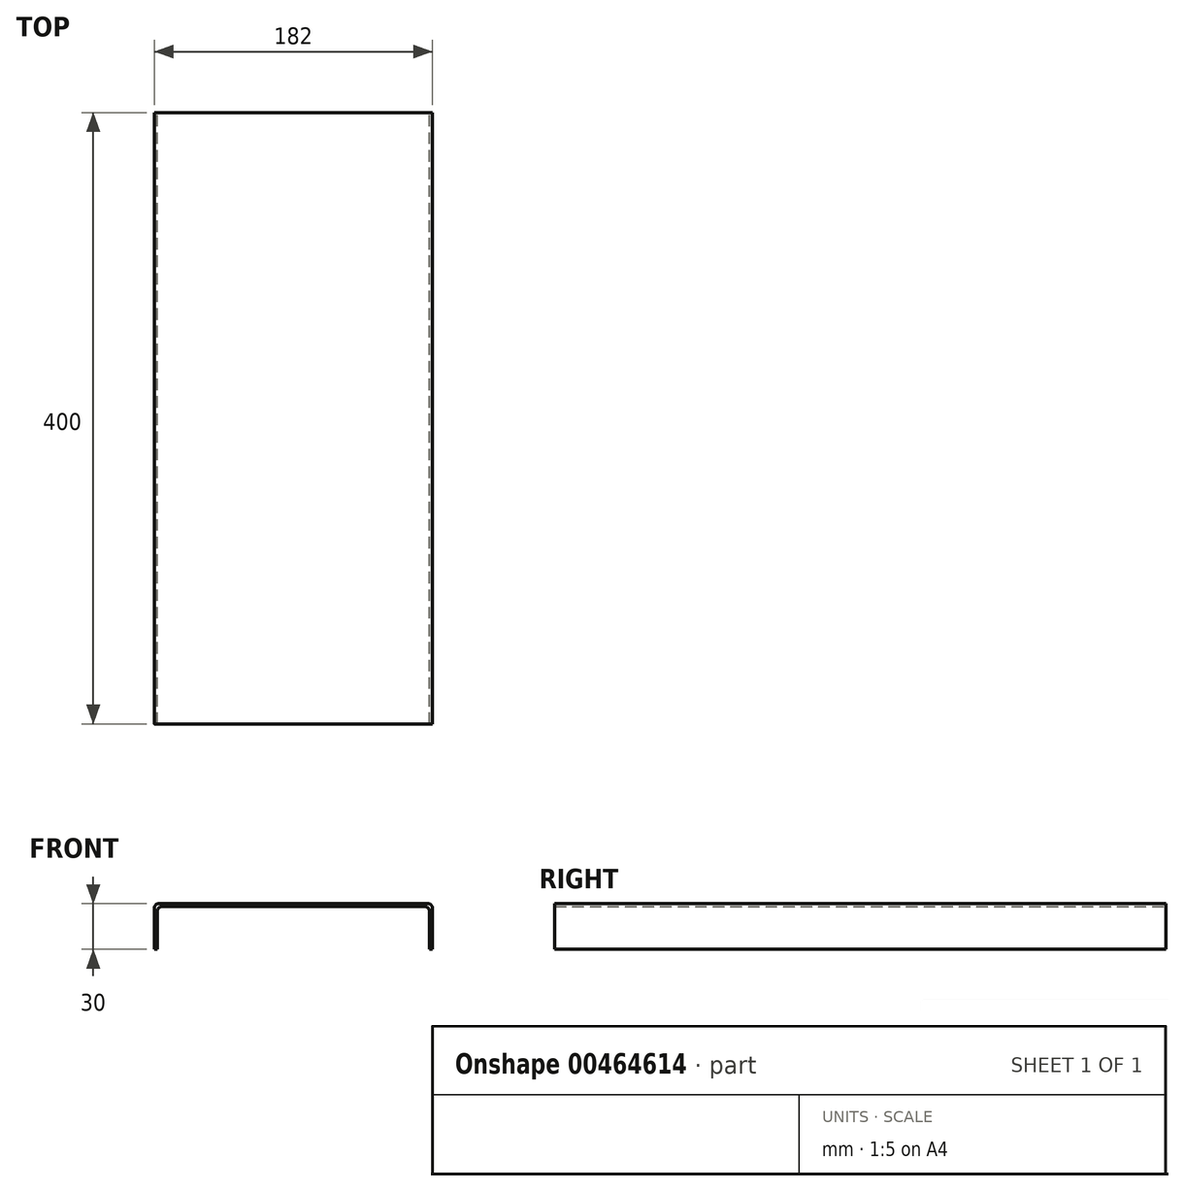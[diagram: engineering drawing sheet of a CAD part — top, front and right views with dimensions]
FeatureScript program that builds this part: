
annotation { "Feature Type Name" : "Feature", "Feature Type Description" : "" }
export const myFeature = defineFeature(function(context is Context, id is Id, definition is map)
    precondition{}
    {
        {
            var Q0;
            Q0=qCreatedBy(makeId("Front.planeOp"),FACE);
            var sketch = newSketch(context, id + "F0", { "sketchPlane" : qUnion([Q0])});
            skLineSegment(sketch, "E0", {"start": v(0, 0) * mm, "end": v(-88, 0) * mm});
            skLineSegment(sketch, "E1", {"start": v(-91, -3) * mm, "end": v(-91, -30) * mm});
            skLineSegment(sketch, "E2.0", {"start": v(-89, -5) * mm, "end": v(-89, -30) * mm});
            skLineSegment(sketch, "E2.1", {"start": v(0, -2) * mm, "end": v(-86, -2) * mm});
            skLineSegment(sketch, "E3", {"start": v(-89, -30) * mm, "end": v(-91, -30) * mm});
            skPoint(sketch, "E4.visualSharp", {"position": v(-89, -2) * mm});
            skArc(sketch, "E4.filletArc", {"start": v(-86, -2) * mm, "mid": v(-88.12, -2.88) * mm, "end": v(-89, -5) * mm});
            skPoint(sketch, "E5.visualSharp", {"position": v(-91, 0) * mm});
            skArc(sketch, "E5.filletArc", {"start": v(-88, 0) * mm, "mid": v(-90.12, -0.88) * mm, "end": v(-91, -3) * mm});
            skArc(sketch, "E6.MirrorCS", {"start": v(88, 0) * mm, "mid": v(90.12, -0.88) * mm, "end": v(91, -3) * mm});
            skArc(sketch, "E7.MirrorCS", {"start": v(86, -2) * mm, "mid": v(88.12, -2.88) * mm, "end": v(89, -5) * mm});
            skLineSegment(sketch, "E8.MirrorCS", {"start": v(89, -30) * mm, "end": v(91, -30) * mm});
            skPoint(sketch, "E9.MirrorP", {"position": v(89, -2) * mm});
            skLineSegment(sketch, "E10.MirrorCS", {"start": v(0, 0) * mm, "end": v(88, 0) * mm});
            skLineSegment(sketch, "E11.MirrorCS", {"start": v(91, -3) * mm, "end": v(91, -30) * mm});
            skLineSegment(sketch, "E12.MirrorCS", {"start": v(89, -5) * mm, "end": v(89, -30) * mm});
            skPoint(sketch, "E13.MirrorP", {"position": v(91, 0) * mm});
            skLineSegment(sketch, "E14.MirrorCS", {"start": v(0, -2) * mm, "end": v(86, -2) * mm});
            skSolve(sketch);
        }
        {
            var Q0;
            Q0 = qSketchRegion(id + "F0", true);
            extrude(context, id + "F1", {"entities" : qUnion([Q0]), "depth" : 400 * mm});
        }
    });
